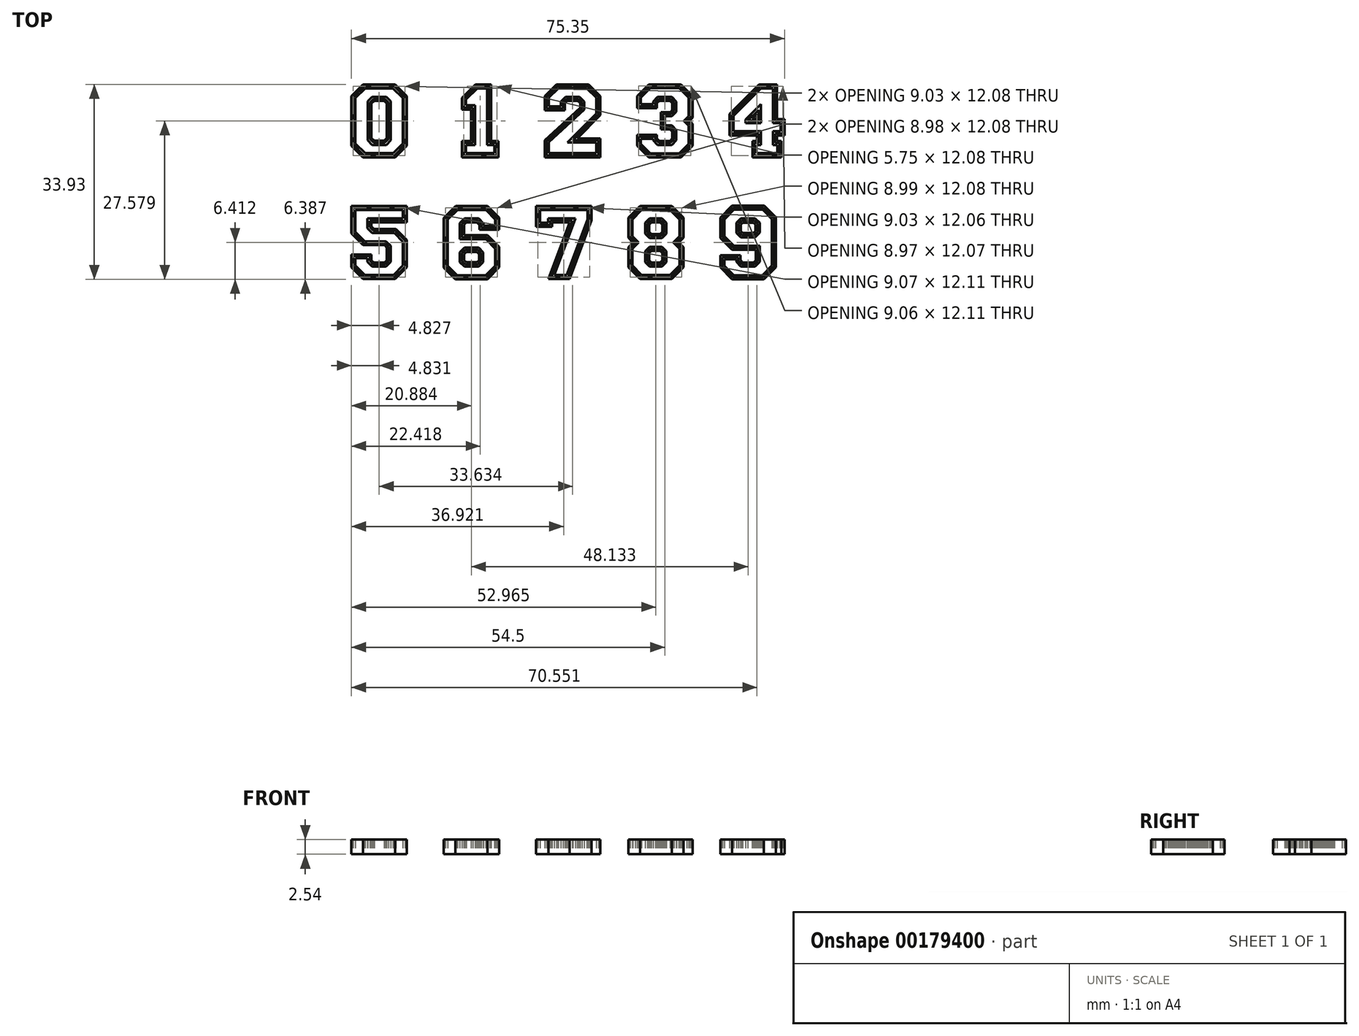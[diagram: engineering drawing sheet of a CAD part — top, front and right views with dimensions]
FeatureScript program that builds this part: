
annotation { "Feature Type Name" : "Feature", "Feature Type Description" : "" }
export const myFeature = defineFeature(function(context is Context, id is Id, definition is map)
    precondition{}
    {
        {
            var Q0;
            Q0=qCreatedBy(makeId("Top.planeOp"),FACE);
            var sketch = newSketch(context, id + "F0", { "sketchPlane" : qUnion([Q0])});
            skLineSegment(sketch, "E0", {"start": v(-43.64, -4.3) * mm, "end": v(-41.6, -2.26) * mm});
            skLineSegment(sketch, "E1", {"start": v(-41.6, -2.26) * mm, "end": v(-36.02, -2.26) * mm});
            skLineSegment(sketch, "E2", {"start": v(-36.02, -2.26) * mm, "end": v(-33.99, -4.3) * mm});
            skLineSegment(sketch, "E3", {"start": v(-33.99, -4.3) * mm, "end": v(-33.99, -12.93) * mm});
            skLineSegment(sketch, "E4", {"start": v(-33.99, -12.93) * mm, "end": v(-36.02, -14.96) * mm});
            skLineSegment(sketch, "E5", {"start": v(-36.02, -14.96) * mm, "end": v(-41.6, -14.96) * mm});
            skLineSegment(sketch, "E6", {"start": v(-41.6, -14.96) * mm, "end": v(-43.64, -12.93) * mm});
            skLineSegment(sketch, "E7", {"start": v(-43.64, -12.93) * mm, "end": v(-43.64, -4.3) * mm});
            skLineSegment(sketch, "E8", {"start": v(-43.33, -4.44) * mm, "end": v(-41.46, -2.57) * mm});
            skLineSegment(sketch, "E9", {"start": v(-41.46, -2.57) * mm, "end": v(-36.17, -2.57) * mm});
            skLineSegment(sketch, "E10", {"start": v(-36.17, -2.57) * mm, "end": v(-34.3, -4.44) * mm});
            skLineSegment(sketch, "E11", {"start": v(-34.3, -4.44) * mm, "end": v(-34.3, -12.78) * mm});
            skLineSegment(sketch, "E12", {"start": v(-34.3, -12.78) * mm, "end": v(-36.17, -14.65) * mm});
            skLineSegment(sketch, "E13", {"start": v(-36.17, -14.65) * mm, "end": v(-41.46, -14.65) * mm});
            skLineSegment(sketch, "E14", {"start": v(-41.46, -14.65) * mm, "end": v(-43.33, -12.78) * mm});
            skLineSegment(sketch, "E15", {"start": v(-43.33, -12.78) * mm, "end": v(-43.33, -4.44) * mm});
            skLineSegment(sketch, "E16", {"start": v(-42.93, -4.64) * mm, "end": v(-41.26, -2.97) * mm});
            skLineSegment(sketch, "E17", {"start": v(-41.26, -2.97) * mm, "end": v(-36.38, -2.97) * mm});
            skLineSegment(sketch, "E18", {"start": v(-36.38, -2.97) * mm, "end": v(-34.68, -4.66) * mm});
            skLineSegment(sketch, "E19", {"start": v(-34.68, -4.66) * mm, "end": v(-34.68, -12.58) * mm});
            skLineSegment(sketch, "E20", {"start": v(-34.68, -12.58) * mm, "end": v(-36.35, -14.25) * mm});
            skLineSegment(sketch, "E21", {"start": v(-36.35, -14.25) * mm, "end": v(-41.26, -14.25) * mm});
            skLineSegment(sketch, "E22", {"start": v(-41.26, -14.25) * mm, "end": v(-42.93, -12.58) * mm});
            skLineSegment(sketch, "E23", {"start": v(-42.93, -12.58) * mm, "end": v(-42.93, -4.64) * mm});
            skLineSegment(sketch, "E24", {"start": v(-40.8, -5.2) * mm, "end": v(-40.06, -4.46) * mm});
            skLineSegment(sketch, "E25", {"start": v(-40.06, -4.46) * mm, "end": v(-37.54, -4.46) * mm});
            skLineSegment(sketch, "E26", {"start": v(-37.54, -4.46) * mm, "end": v(-36.8, -5.2) * mm});
            skLineSegment(sketch, "E27", {"start": v(-36.8, -5.2) * mm, "end": v(-36.8, -12.02) * mm});
            skLineSegment(sketch, "E28", {"start": v(-36.8, -12.02) * mm, "end": v(-37.58, -12.8) * mm});
            skLineSegment(sketch, "E29", {"start": v(-37.58, -12.8) * mm, "end": v(-40.03, -12.8) * mm});
            skLineSegment(sketch, "E30", {"start": v(-40.03, -12.8) * mm, "end": v(-40.8, -12.02) * mm});
            skLineSegment(sketch, "E31", {"start": v(-40.8, -12.02) * mm, "end": v(-40.8, -5.2) * mm});
            skLineSegment(sketch, "E32", {"start": v(-40.45, -5.46) * mm, "end": v(-39.81, -4.82) * mm});
            skLineSegment(sketch, "E33", {"start": v(-39.81, -4.82) * mm, "end": v(-37.82, -4.82) * mm});
            skLineSegment(sketch, "E34", {"start": v(-37.82, -4.82) * mm, "end": v(-37.18, -5.46) * mm});
            skLineSegment(sketch, "E35", {"start": v(-37.18, -5.46) * mm, "end": v(-37.18, -11.77) * mm});
            skLineSegment(sketch, "E36", {"start": v(-37.18, -11.77) * mm, "end": v(-37.82, -12.4) * mm});
            skLineSegment(sketch, "E37", {"start": v(-37.82, -12.4) * mm, "end": v(-39.81, -12.4) * mm});
            skLineSegment(sketch, "E38", {"start": v(-39.81, -12.4) * mm, "end": v(-40.45, -11.77) * mm});
            skLineSegment(sketch, "E39", {"start": v(-40.45, -11.77) * mm, "end": v(-40.45, -5.46) * mm});
            skLineSegment(sketch, "E40", {"start": v(-40.14, -5.58) * mm, "end": v(-39.68, -5.13) * mm});
            skLineSegment(sketch, "E41", {"start": v(-39.68, -5.13) * mm, "end": v(-37.94, -5.13) * mm});
            skLineSegment(sketch, "E42", {"start": v(-37.94, -5.13) * mm, "end": v(-37.49, -5.58) * mm});
            skLineSegment(sketch, "E43", {"start": v(-37.49, -5.58) * mm, "end": v(-37.49, -11.64) * mm});
            skLineSegment(sketch, "E44", {"start": v(-37.49, -11.64) * mm, "end": v(-37.94, -12.1) * mm});
            skLineSegment(sketch, "E45", {"start": v(-37.94, -12.1) * mm, "end": v(-39.68, -12.1) * mm});
            skLineSegment(sketch, "E46", {"start": v(-39.68, -12.1) * mm, "end": v(-40.14, -11.64) * mm});
            skLineSegment(sketch, "E47", {"start": v(-40.14, -11.64) * mm, "end": v(-40.14, -5.58) * mm});
            skLineSegment(sketch, "E48", {"start": v(-19.33, -2.26) * mm, "end": v(-19.33, -12.11) * mm});
            skLineSegment(sketch, "E49", {"start": v(-19.33, -12.11) * mm, "end": v(-18.06, -12.11) * mm});
            skLineSegment(sketch, "E50", {"start": v(-18.06, -12.11) * mm, "end": v(-18.06, -14.96) * mm});
            skLineSegment(sketch, "E51", {"start": v(-18.06, -14.96) * mm, "end": v(-24.4, -14.96) * mm});
            skLineSegment(sketch, "E52", {"start": v(-24.4, -14.96) * mm, "end": v(-24.4, -12.11) * mm});
            skLineSegment(sketch, "E53", {"start": v(-24.4, -12.11) * mm, "end": v(-22.8, -12.11) * mm});
            skLineSegment(sketch, "E54", {"start": v(-22.8, -12.11) * mm, "end": v(-22.8, -6.64) * mm});
            skLineSegment(sketch, "E55", {"start": v(-22.8, -6.64) * mm, "end": v(-24.4, -6.64) * mm});
            skLineSegment(sketch, "E56", {"start": v(-24.4, -6.64) * mm, "end": v(-24.4, -4.62) * mm});
            skLineSegment(sketch, "E57", {"start": v(-24.4, -4.62) * mm, "end": v(-22.05, -2.26) * mm});
            skLineSegment(sketch, "E58", {"start": v(-22.05, -2.26) * mm, "end": v(-19.33, -2.26) * mm});
            skLineSegment(sketch, "E59", {"start": v(-19.62, -2.57) * mm, "end": v(-19.62, -12.42) * mm});
            skLineSegment(sketch, "E60", {"start": v(-19.62, -12.42) * mm, "end": v(-18.35, -12.42) * mm});
            skLineSegment(sketch, "E61", {"start": v(-18.35, -12.42) * mm, "end": v(-18.35, -14.65) * mm});
            skLineSegment(sketch, "E62", {"start": v(-18.35, -14.65) * mm, "end": v(-24.1, -14.65) * mm});
            skLineSegment(sketch, "E63", {"start": v(-24.1, -14.65) * mm, "end": v(-24.1, -12.42) * mm});
            skLineSegment(sketch, "E64", {"start": v(-24.1, -12.42) * mm, "end": v(-22.5, -12.42) * mm});
            skLineSegment(sketch, "E65", {"start": v(-22.5, -12.42) * mm, "end": v(-22.5, -6.33) * mm});
            skLineSegment(sketch, "E66", {"start": v(-22.5, -6.33) * mm, "end": v(-24.1, -6.33) * mm});
            skLineSegment(sketch, "E67", {"start": v(-24.1, -6.33) * mm, "end": v(-24.1, -4.75) * mm});
            skLineSegment(sketch, "E68", {"start": v(-24.1, -4.75) * mm, "end": v(-21.92, -2.57) * mm});
            skLineSegment(sketch, "E69", {"start": v(-21.92, -2.57) * mm, "end": v(-19.62, -2.57) * mm});
            skLineSegment(sketch, "E70", {"start": v(-20.01, -2.97) * mm, "end": v(-20.01, -12.82) * mm});
            skLineSegment(sketch, "E71", {"start": v(-20.01, -12.82) * mm, "end": v(-18.74, -12.82) * mm});
            skLineSegment(sketch, "E72", {"start": v(-18.74, -12.82) * mm, "end": v(-18.74, -14.25) * mm});
            skLineSegment(sketch, "E73", {"start": v(-18.74, -14.25) * mm, "end": v(-23.7, -14.25) * mm});
            skLineSegment(sketch, "E74", {"start": v(-23.7, -14.25) * mm, "end": v(-23.7, -12.82) * mm});
            skLineSegment(sketch, "E75", {"start": v(-23.7, -12.82) * mm, "end": v(-22.1, -12.82) * mm});
            skLineSegment(sketch, "E76", {"start": v(-22.1, -12.82) * mm, "end": v(-22.1, -5.93) * mm});
            skLineSegment(sketch, "E77", {"start": v(-22.1, -5.93) * mm, "end": v(-23.7, -5.93) * mm});
            skLineSegment(sketch, "E78", {"start": v(-23.7, -5.93) * mm, "end": v(-23.7, -4.91) * mm});
            skLineSegment(sketch, "E79", {"start": v(-23.7, -4.91) * mm, "end": v(-21.76, -2.97) * mm});
            skLineSegment(sketch, "E80", {"start": v(-21.76, -2.97) * mm, "end": v(-20.01, -2.97) * mm});
            skLineSegment(sketch, "E81", {"start": v(22.6, -23.39) * mm, "end": v(28.18, -23.39) * mm});
            skLineSegment(sketch, "E82", {"start": v(28.18, -23.39) * mm, "end": v(30.22, -25.43) * mm});
            skLineSegment(sketch, "E83", {"start": v(30.22, -25.43) * mm, "end": v(30.22, -34.07) * mm});
            skLineSegment(sketch, "E84", {"start": v(30.22, -34.07) * mm, "end": v(28.12, -36.17) * mm});
            skLineSegment(sketch, "E85", {"start": v(28.12, -36.17) * mm, "end": v(22.57, -36.17) * mm});
            skLineSegment(sketch, "E86", {"start": v(22.57, -36.17) * mm, "end": v(20.53, -34.1) * mm});
            skLineSegment(sketch, "E87", {"start": v(20.53, -34.1) * mm, "end": v(20.53, -32.02) * mm});
            skLineSegment(sketch, "E88", {"start": v(20.53, -32.02) * mm, "end": v(24.02, -32.02) * mm});
            skLineSegment(sketch, "E89", {"start": v(24.02, -32.02) * mm, "end": v(24.02, -32.85) * mm});
            skLineSegment(sketch, "E90", {"start": v(24.02, -32.85) * mm, "end": v(24.42, -33.27) * mm});
            skLineSegment(sketch, "E91", {"start": v(24.42, -33.27) * mm, "end": v(26.3, -33.27) * mm});
            skLineSegment(sketch, "E92", {"start": v(26.3, -33.27) * mm, "end": v(26.68, -32.88) * mm});
            skLineSegment(sketch, "E93", {"start": v(26.68, -32.88) * mm, "end": v(26.68, -31.05) * mm});
            skLineSegment(sketch, "E94", {"start": v(26.68, -31.05) * mm, "end": v(22.58, -31.05) * mm});
            skLineSegment(sketch, "E95", {"start": v(22.58, -31.05) * mm, "end": v(20.54, -29.01) * mm});
            skLineSegment(sketch, "E96", {"start": v(20.54, -29.01) * mm, "end": v(20.54, -25.46) * mm});
            skLineSegment(sketch, "E97", {"start": v(20.54, -25.46) * mm, "end": v(22.6, -23.39) * mm});
            skLineSegment(sketch, "E98", {"start": v(22.75, -23.74) * mm, "end": v(28.03, -23.74) * mm});
            skLineSegment(sketch, "E99", {"start": v(28.03, -23.74) * mm, "end": v(29.87, -25.58) * mm});
            skLineSegment(sketch, "E100", {"start": v(29.87, -25.58) * mm, "end": v(29.87, -33.92) * mm});
            skLineSegment(sketch, "E101", {"start": v(29.87, -33.92) * mm, "end": v(27.97, -35.82) * mm});
            skLineSegment(sketch, "E102", {"start": v(27.97, -35.82) * mm, "end": v(22.72, -35.82) * mm});
            skLineSegment(sketch, "E103", {"start": v(22.72, -35.82) * mm, "end": v(20.89, -33.96) * mm});
            skLineSegment(sketch, "E104", {"start": v(20.89, -33.96) * mm, "end": v(20.89, -32.37) * mm});
            skLineSegment(sketch, "E105", {"start": v(20.89, -32.37) * mm, "end": v(23.67, -32.37) * mm});
            skLineSegment(sketch, "E106", {"start": v(23.67, -32.37) * mm, "end": v(23.67, -33) * mm});
            skLineSegment(sketch, "E107", {"start": v(23.67, -33) * mm, "end": v(24.27, -33.62) * mm});
            skLineSegment(sketch, "E108", {"start": v(24.27, -33.62) * mm, "end": v(26.46, -33.62) * mm});
            skLineSegment(sketch, "E109", {"start": v(26.46, -33.62) * mm, "end": v(27.04, -33.03) * mm});
            skLineSegment(sketch, "E110", {"start": v(27.04, -33.03) * mm, "end": v(27.04, -30.7) * mm});
            skLineSegment(sketch, "E111", {"start": v(27.04, -30.7) * mm, "end": v(22.72, -30.7) * mm});
            skLineSegment(sketch, "E112", {"start": v(22.72, -30.7) * mm, "end": v(20.9, -28.87) * mm});
            skLineSegment(sketch, "E113", {"start": v(20.9, -28.87) * mm, "end": v(20.9, -25.6) * mm});
            skLineSegment(sketch, "E114", {"start": v(20.9, -25.6) * mm, "end": v(22.75, -23.74) * mm});
            skLineSegment(sketch, "E115", {"start": v(22.9, -24.1) * mm, "end": v(27.89, -24.1) * mm});
            skLineSegment(sketch, "E116", {"start": v(27.89, -24.1) * mm, "end": v(29.51, -25.72) * mm});
            skLineSegment(sketch, "E117", {"start": v(29.51, -25.72) * mm, "end": v(29.51, -33.78) * mm});
            skLineSegment(sketch, "E118", {"start": v(29.51, -33.78) * mm, "end": v(27.82, -35.47) * mm});
            skLineSegment(sketch, "E119", {"start": v(27.82, -35.47) * mm, "end": v(22.87, -35.47) * mm});
            skLineSegment(sketch, "E120", {"start": v(22.87, -35.47) * mm, "end": v(21.24, -33.81) * mm});
            skLineSegment(sketch, "E121", {"start": v(21.24, -33.81) * mm, "end": v(21.24, -32.73) * mm});
            skLineSegment(sketch, "E122", {"start": v(21.24, -32.73) * mm, "end": v(23.31, -32.73) * mm});
            skLineSegment(sketch, "E123", {"start": v(23.31, -32.73) * mm, "end": v(23.31, -33.13) * mm});
            skLineSegment(sketch, "E124", {"start": v(23.31, -33.13) * mm, "end": v(24.12, -33.97) * mm});
            skLineSegment(sketch, "E125", {"start": v(24.12, -33.97) * mm, "end": v(26.6, -33.97) * mm});
            skLineSegment(sketch, "E126", {"start": v(26.6, -33.97) * mm, "end": v(27.39, -33.17) * mm});
            skLineSegment(sketch, "E127", {"start": v(27.39, -33.17) * mm, "end": v(27.39, -30.35) * mm});
            skLineSegment(sketch, "E128", {"start": v(27.39, -30.35) * mm, "end": v(22.87, -30.35) * mm});
            skLineSegment(sketch, "E129", {"start": v(22.87, -30.35) * mm, "end": v(21.25, -28.72) * mm});
            skLineSegment(sketch, "E130", {"start": v(21.25, -28.72) * mm, "end": v(21.25, -25.75) * mm});
            skLineSegment(sketch, "E131", {"start": v(21.25, -25.75) * mm, "end": v(22.9, -24.1) * mm});
            skLineSegment(sketch, "E132", {"start": v(24.12, -25.6) * mm, "end": v(26.6, -25.6) * mm});
            skLineSegment(sketch, "E133", {"start": v(26.6, -25.6) * mm, "end": v(27.4, -26.37) * mm});
            skLineSegment(sketch, "E134", {"start": v(27.4, -26.37) * mm, "end": v(27.4, -28.1) * mm});
            skLineSegment(sketch, "E135", {"start": v(27.4, -28.1) * mm, "end": v(26.6, -28.89) * mm});
            skLineSegment(sketch, "E136", {"start": v(26.6, -28.89) * mm, "end": v(24.11, -28.89) * mm});
            skLineSegment(sketch, "E137", {"start": v(24.11, -28.89) * mm, "end": v(23.33, -28.1) * mm});
            skLineSegment(sketch, "E138", {"start": v(23.33, -28.1) * mm, "end": v(23.33, -26.37) * mm});
            skLineSegment(sketch, "E139", {"start": v(23.33, -26.37) * mm, "end": v(24.12, -25.6) * mm});
            skLineSegment(sketch, "E140", {"start": v(24.27, -25.98) * mm, "end": v(26.45, -25.98) * mm});
            skLineSegment(sketch, "E141", {"start": v(26.45, -25.98) * mm, "end": v(27.02, -26.53) * mm});
            skLineSegment(sketch, "E142", {"start": v(27.02, -26.53) * mm, "end": v(27.02, -27.94) * mm});
            skLineSegment(sketch, "E143", {"start": v(27.02, -27.94) * mm, "end": v(26.44, -28.52) * mm});
            skLineSegment(sketch, "E144", {"start": v(26.44, -28.52) * mm, "end": v(24.27, -28.52) * mm});
            skLineSegment(sketch, "E145", {"start": v(24.27, -28.52) * mm, "end": v(23.7, -27.95) * mm});
            skLineSegment(sketch, "E146", {"start": v(23.7, -27.95) * mm, "end": v(23.7, -26.53) * mm});
            skLineSegment(sketch, "E147", {"start": v(23.7, -26.53) * mm, "end": v(24.27, -25.98) * mm});
            skLineSegment(sketch, "E148", {"start": v(24.42, -26.36) * mm, "end": v(26.3, -26.36) * mm});
            skLineSegment(sketch, "E149", {"start": v(26.3, -26.36) * mm, "end": v(26.65, -26.69) * mm});
            skLineSegment(sketch, "E150", {"start": v(26.65, -26.69) * mm, "end": v(26.65, -27.78) * mm});
            skLineSegment(sketch, "E151", {"start": v(26.65, -27.78) * mm, "end": v(26.29, -28.14) * mm});
            skLineSegment(sketch, "E152", {"start": v(26.29, -28.14) * mm, "end": v(24.42, -28.14) * mm});
            skLineSegment(sketch, "E153", {"start": v(24.42, -28.14) * mm, "end": v(24.08, -27.8) * mm});
            skLineSegment(sketch, "E154", {"start": v(24.08, -27.8) * mm, "end": v(24.08, -26.68) * mm});
            skLineSegment(sketch, "E155", {"start": v(24.08, -26.68) * mm, "end": v(24.42, -26.36) * mm});
            skLineSegment(sketch, "E156", {"start": v(-19.98, -36.2) * mm, "end": v(-25.56, -36.2) * mm});
            skLineSegment(sketch, "E157", {"start": v(-25.56, -36.2) * mm, "end": v(-27.6, -34.15) * mm});
            skLineSegment(sketch, "E158", {"start": v(-27.6, -34.15) * mm, "end": v(-27.6, -25.52) * mm});
            skLineSegment(sketch, "E159", {"start": v(-27.6, -25.52) * mm, "end": v(-25.5, -23.41) * mm});
            skLineSegment(sketch, "E160", {"start": v(-25.5, -23.41) * mm, "end": v(-19.95, -23.41) * mm});
            skLineSegment(sketch, "E161", {"start": v(-19.95, -23.41) * mm, "end": v(-17.91, -25.48) * mm});
            skLineSegment(sketch, "E162", {"start": v(-17.91, -25.48) * mm, "end": v(-17.91, -27.56) * mm});
            skLineSegment(sketch, "E163", {"start": v(-17.91, -27.56) * mm, "end": v(-21.4, -27.56) * mm});
            skLineSegment(sketch, "E164", {"start": v(-21.4, -27.56) * mm, "end": v(-21.4, -26.73) * mm});
            skLineSegment(sketch, "E165", {"start": v(-21.4, -26.73) * mm, "end": v(-21.8, -26.32) * mm});
            skLineSegment(sketch, "E166", {"start": v(-21.8, -26.32) * mm, "end": v(-23.69, -26.32) * mm});
            skLineSegment(sketch, "E167", {"start": v(-23.69, -26.32) * mm, "end": v(-24.06, -26.7) * mm});
            skLineSegment(sketch, "E168", {"start": v(-24.06, -26.7) * mm, "end": v(-24.06, -28.53) * mm});
            skLineSegment(sketch, "E169", {"start": v(-24.06, -28.53) * mm, "end": v(-19.96, -28.53) * mm});
            skLineSegment(sketch, "E170", {"start": v(-19.96, -28.53) * mm, "end": v(-17.92, -30.57) * mm});
            skLineSegment(sketch, "E171", {"start": v(-17.92, -30.57) * mm, "end": v(-17.92, -34.12) * mm});
            skLineSegment(sketch, "E172", {"start": v(-17.92, -34.12) * mm, "end": v(-19.98, -36.2) * mm});
            skLineSegment(sketch, "E173", {"start": v(-20.13, -35.84) * mm, "end": v(-25.41, -35.84) * mm});
            skLineSegment(sketch, "E174", {"start": v(-25.41, -35.84) * mm, "end": v(-27.25, -34) * mm});
            skLineSegment(sketch, "E175", {"start": v(-27.25, -34) * mm, "end": v(-27.25, -25.66) * mm});
            skLineSegment(sketch, "E176", {"start": v(-27.25, -25.66) * mm, "end": v(-25.35, -23.77) * mm});
            skLineSegment(sketch, "E177", {"start": v(-25.35, -23.77) * mm, "end": v(-20.1, -23.77) * mm});
            skLineSegment(sketch, "E178", {"start": v(-20.1, -23.77) * mm, "end": v(-18.27, -25.63) * mm});
            skLineSegment(sketch, "E179", {"start": v(-18.27, -25.63) * mm, "end": v(-18.27, -27.2) * mm});
            skLineSegment(sketch, "E180", {"start": v(-18.27, -27.2) * mm, "end": v(-21.05, -27.2) * mm});
            skLineSegment(sketch, "E181", {"start": v(-21.05, -27.2) * mm, "end": v(-21.05, -26.6) * mm});
            skLineSegment(sketch, "E182", {"start": v(-21.05, -26.6) * mm, "end": v(-21.65, -25.96) * mm});
            skLineSegment(sketch, "E183", {"start": v(-21.65, -25.96) * mm, "end": v(-23.84, -25.96) * mm});
            skLineSegment(sketch, "E184", {"start": v(-23.84, -25.96) * mm, "end": v(-24.42, -26.56) * mm});
            skLineSegment(sketch, "E185", {"start": v(-24.42, -26.56) * mm, "end": v(-24.42, -28.88) * mm});
            skLineSegment(sketch, "E186", {"start": v(-24.42, -28.88) * mm, "end": v(-20.1, -28.88) * mm});
            skLineSegment(sketch, "E187", {"start": v(-20.1, -28.88) * mm, "end": v(-18.27, -30.71) * mm});
            skLineSegment(sketch, "E188", {"start": v(-18.27, -30.71) * mm, "end": v(-18.27, -33.98) * mm});
            skLineSegment(sketch, "E189", {"start": v(-18.27, -33.98) * mm, "end": v(-20.13, -35.84) * mm});
            skLineSegment(sketch, "E190", {"start": v(-20.27, -35.49) * mm, "end": v(-25.27, -35.49) * mm});
            skLineSegment(sketch, "E191", {"start": v(-25.27, -35.49) * mm, "end": v(-26.9, -33.86) * mm});
            skLineSegment(sketch, "E192", {"start": v(-26.9, -33.86) * mm, "end": v(-26.9, -25.8) * mm});
            skLineSegment(sketch, "E193", {"start": v(-26.9, -25.8) * mm, "end": v(-25.2, -24.12) * mm});
            skLineSegment(sketch, "E194", {"start": v(-25.2, -24.12) * mm, "end": v(-20.25, -24.12) * mm});
            skLineSegment(sketch, "E195", {"start": v(-20.25, -24.12) * mm, "end": v(-18.62, -25.77) * mm});
            skLineSegment(sketch, "E196", {"start": v(-18.62, -25.77) * mm, "end": v(-18.62, -26.86) * mm});
            skLineSegment(sketch, "E197", {"start": v(-18.62, -26.86) * mm, "end": v(-20.7, -26.86) * mm});
            skLineSegment(sketch, "E198", {"start": v(-20.7, -26.86) * mm, "end": v(-20.7, -26.45) * mm});
            skLineSegment(sketch, "E199", {"start": v(-20.7, -26.45) * mm, "end": v(-21.5, -25.61) * mm});
            skLineSegment(sketch, "E200", {"start": v(-21.5, -25.61) * mm, "end": v(-23.98, -25.61) * mm});
            skLineSegment(sketch, "E201", {"start": v(-23.98, -25.61) * mm, "end": v(-24.77, -26.41) * mm});
            skLineSegment(sketch, "E202", {"start": v(-24.77, -26.41) * mm, "end": v(-24.77, -29.24) * mm});
            skLineSegment(sketch, "E203", {"start": v(-24.77, -29.24) * mm, "end": v(-20.25, -29.24) * mm});
            skLineSegment(sketch, "E204", {"start": v(-20.25, -29.24) * mm, "end": v(-18.62, -30.86) * mm});
            skLineSegment(sketch, "E205", {"start": v(-18.62, -30.86) * mm, "end": v(-18.62, -33.83) * mm});
            skLineSegment(sketch, "E206", {"start": v(-18.62, -33.83) * mm, "end": v(-20.27, -35.49) * mm});
            skLineSegment(sketch, "E207", {"start": v(-21.5, -33.98) * mm, "end": v(-23.98, -33.98) * mm});
            skLineSegment(sketch, "E208", {"start": v(-23.98, -33.98) * mm, "end": v(-24.78, -33.22) * mm});
            skLineSegment(sketch, "E209", {"start": v(-24.78, -33.22) * mm, "end": v(-24.78, -31.5) * mm});
            skLineSegment(sketch, "E210", {"start": v(-24.78, -31.5) * mm, "end": v(-23.98, -30.7) * mm});
            skLineSegment(sketch, "E211", {"start": v(-23.98, -30.7) * mm, "end": v(-21.5, -30.7) * mm});
            skLineSegment(sketch, "E212", {"start": v(-21.5, -30.7) * mm, "end": v(-20.71, -31.47) * mm});
            skLineSegment(sketch, "E213", {"start": v(-20.71, -31.47) * mm, "end": v(-20.71, -33.22) * mm});
            skLineSegment(sketch, "E214", {"start": v(-20.71, -33.22) * mm, "end": v(-21.5, -33.98) * mm});
            skLineSegment(sketch, "E215", {"start": v(-21.65, -33.6) * mm, "end": v(-23.83, -33.6) * mm});
            skLineSegment(sketch, "E216", {"start": v(-23.83, -33.6) * mm, "end": v(-24.4, -33.05) * mm});
            skLineSegment(sketch, "E217", {"start": v(-24.4, -33.05) * mm, "end": v(-24.4, -31.65) * mm});
            skLineSegment(sketch, "E218", {"start": v(-24.4, -31.65) * mm, "end": v(-23.82, -31.07) * mm});
            skLineSegment(sketch, "E219", {"start": v(-23.82, -31.07) * mm, "end": v(-21.65, -31.07) * mm});
            skLineSegment(sketch, "E220", {"start": v(-21.65, -31.07) * mm, "end": v(-21.09, -31.63) * mm});
            skLineSegment(sketch, "E221", {"start": v(-21.09, -31.63) * mm, "end": v(-21.09, -33.06) * mm});
            skLineSegment(sketch, "E222", {"start": v(-21.09, -33.06) * mm, "end": v(-21.65, -33.6) * mm});
            skLineSegment(sketch, "E223", {"start": v(-21.8, -33.23) * mm, "end": v(-23.68, -33.23) * mm});
            skLineSegment(sketch, "E224", {"start": v(-23.68, -33.23) * mm, "end": v(-24.03, -32.9) * mm});
            skLineSegment(sketch, "E225", {"start": v(-24.03, -32.9) * mm, "end": v(-24.03, -31.8) * mm});
            skLineSegment(sketch, "E226", {"start": v(-24.03, -31.8) * mm, "end": v(-23.67, -31.44) * mm});
            skLineSegment(sketch, "E227", {"start": v(-23.67, -31.44) * mm, "end": v(-21.8, -31.44) * mm});
            skLineSegment(sketch, "E228", {"start": v(-21.8, -31.44) * mm, "end": v(-21.46, -31.78) * mm});
            skLineSegment(sketch, "E229", {"start": v(-21.46, -31.78) * mm, "end": v(-21.46, -32.9) * mm});
            skLineSegment(sketch, "E230", {"start": v(-21.46, -32.9) * mm, "end": v(-21.8, -33.23) * mm});
            skLineSegment(sketch, "E231", {"start": v(-10, -6.82) * mm, "end": v(-10, -4.3) * mm});
            skLineSegment(sketch, "E232", {"start": v(-10, -4.3) * mm, "end": v(-7.97, -2.26) * mm});
            skLineSegment(sketch, "E233", {"start": v(-7.97, -2.26) * mm, "end": v(-2.39, -2.26) * mm});
            skLineSegment(sketch, "E234", {"start": v(-2.39, -2.26) * mm, "end": v(-0.35, -4.3) * mm});
            skLineSegment(sketch, "E235", {"start": v(-0.35, -4.3) * mm, "end": v(-0.35, -7.65) * mm});
            skLineSegment(sketch, "E236", {"start": v(-0.35, -7.65) * mm, "end": v(-4.38, -11.68) * mm});
            skLineSegment(sketch, "E237", {"start": v(-4.38, -11.68) * mm, "end": v(-0.35, -11.68) * mm});
            skLineSegment(sketch, "E238", {"start": v(-0.35, -11.68) * mm, "end": v(-0.35, -14.96) * mm});
            skLineSegment(sketch, "E239", {"start": v(-0.35, -14.96) * mm, "end": v(-10, -14.96) * mm});
            skLineSegment(sketch, "E240", {"start": v(-10, -14.96) * mm, "end": v(-10, -12) * mm});
            skLineSegment(sketch, "E241", {"start": v(-10, -12) * mm, "end": v(-3.85, -6.36) * mm});
            skLineSegment(sketch, "E242", {"start": v(-3.85, -6.36) * mm, "end": v(-3.85, -5.55) * mm});
            skLineSegment(sketch, "E243", {"start": v(-3.85, -5.55) * mm, "end": v(-4.27, -5.13) * mm});
            skLineSegment(sketch, "E244", {"start": v(-4.27, -5.13) * mm, "end": v(-6.1, -5.13) * mm});
            skLineSegment(sketch, "E245", {"start": v(-6.1, -5.13) * mm, "end": v(-6.52, -5.55) * mm});
            skLineSegment(sketch, "E246", {"start": v(-6.52, -5.55) * mm, "end": v(-6.52, -6.82) * mm});
            skLineSegment(sketch, "E247", {"start": v(-6.52, -6.82) * mm, "end": v(-10, -6.82) * mm});
            skLineSegment(sketch, "E248", {"start": v(-9.7, -6.5) * mm, "end": v(-9.7, -4.42) * mm});
            skLineSegment(sketch, "E249", {"start": v(-9.7, -4.42) * mm, "end": v(-7.84, -2.57) * mm});
            skLineSegment(sketch, "E250", {"start": v(-7.84, -2.57) * mm, "end": v(-2.51, -2.57) * mm});
            skLineSegment(sketch, "E251", {"start": v(-2.51, -2.57) * mm, "end": v(-0.66, -4.42) * mm});
            skLineSegment(sketch, "E252", {"start": v(-0.66, -4.42) * mm, "end": v(-0.66, -7.52) * mm});
            skLineSegment(sketch, "E253", {"start": v(-0.66, -7.52) * mm, "end": v(-5.12, -11.98) * mm});
            skLineSegment(sketch, "E254", {"start": v(-5.12, -11.98) * mm, "end": v(-0.66, -11.98) * mm});
            skLineSegment(sketch, "E255", {"start": v(-0.66, -11.98) * mm, "end": v(-0.66, -14.65) * mm});
            skLineSegment(sketch, "E256", {"start": v(-0.66, -14.65) * mm, "end": v(-9.7, -14.65) * mm});
            skLineSegment(sketch, "E257", {"start": v(-9.7, -14.65) * mm, "end": v(-9.7, -12.14) * mm});
            skLineSegment(sketch, "E258", {"start": v(-9.7, -12.14) * mm, "end": v(-3.55, -6.5) * mm});
            skLineSegment(sketch, "E259", {"start": v(-3.55, -6.5) * mm, "end": v(-3.55, -5.42) * mm});
            skLineSegment(sketch, "E260", {"start": v(-3.55, -5.42) * mm, "end": v(-4.14, -4.82) * mm});
            skLineSegment(sketch, "E261", {"start": v(-4.14, -4.82) * mm, "end": v(-6.23, -4.82) * mm});
            skLineSegment(sketch, "E262", {"start": v(-6.23, -4.82) * mm, "end": v(-6.83, -5.42) * mm});
            skLineSegment(sketch, "E263", {"start": v(-6.83, -5.42) * mm, "end": v(-6.83, -6.5) * mm});
            skLineSegment(sketch, "E264", {"start": v(-6.83, -6.5) * mm, "end": v(-9.7, -6.5) * mm});
            skLineSegment(sketch, "E265", {"start": v(-9.3, -6.1) * mm, "end": v(-9.3, -4.59) * mm});
            skLineSegment(sketch, "E266", {"start": v(-9.3, -4.59) * mm, "end": v(-7.68, -2.97) * mm});
            skLineSegment(sketch, "E267", {"start": v(-7.68, -2.97) * mm, "end": v(-2.68, -2.97) * mm});
            skLineSegment(sketch, "E268", {"start": v(-2.68, -2.97) * mm, "end": v(-1.06, -4.59) * mm});
            skLineSegment(sketch, "E269", {"start": v(-1.06, -4.59) * mm, "end": v(-1.06, -7.36) * mm});
            skLineSegment(sketch, "E270", {"start": v(-1.06, -7.36) * mm, "end": v(-6.08, -12.38) * mm});
            skLineSegment(sketch, "E271", {"start": v(-6.08, -12.38) * mm, "end": v(-1.06, -12.38) * mm});
            skLineSegment(sketch, "E272", {"start": v(-1.06, -12.38) * mm, "end": v(-1.06, -14.25) * mm});
            skLineSegment(sketch, "E273", {"start": v(-1.06, -14.25) * mm, "end": v(-9.3, -14.25) * mm});
            skLineSegment(sketch, "E274", {"start": v(-9.3, -14.25) * mm, "end": v(-9.3, -12.31) * mm});
            skLineSegment(sketch, "E275", {"start": v(-9.3, -12.31) * mm, "end": v(-3.15, -6.67) * mm});
            skLineSegment(sketch, "E276", {"start": v(-3.15, -6.67) * mm, "end": v(-3.15, -5.25) * mm});
            skLineSegment(sketch, "E277", {"start": v(-3.15, -5.25) * mm, "end": v(-3.98, -4.42) * mm});
            skLineSegment(sketch, "E278", {"start": v(-3.98, -4.42) * mm, "end": v(-6.4, -4.42) * mm});
            skLineSegment(sketch, "E279", {"start": v(-6.4, -4.42) * mm, "end": v(-7.23, -5.25) * mm});
            skLineSegment(sketch, "E280", {"start": v(-7.23, -5.25) * mm, "end": v(-7.23, -6.1) * mm});
            skLineSegment(sketch, "E281", {"start": v(-7.23, -6.1) * mm, "end": v(-9.3, -6.1) * mm});
            skLineSegment(sketch, "E282", {"start": v(6.03, -6.4) * mm, "end": v(6.03, -4.3) * mm});
            skLineSegment(sketch, "E283", {"start": v(6.03, -4.3) * mm, "end": v(8.07, -2.26) * mm});
            skLineSegment(sketch, "E284", {"start": v(8.07, -2.26) * mm, "end": v(13.65, -2.26) * mm});
            skLineSegment(sketch, "E285", {"start": v(13.65, -2.26) * mm, "end": v(15.69, -4.3) * mm});
            skLineSegment(sketch, "E286", {"start": v(15.69, -4.3) * mm, "end": v(15.69, -8.07) * mm});
            skLineSegment(sketch, "E287", {"start": v(15.69, -8.07) * mm, "end": v(15.14, -8.61) * mm});
            skLineSegment(sketch, "E288", {"start": v(15.14, -8.61) * mm, "end": v(15.69, -9.16) * mm});
            skLineSegment(sketch, "E289", {"start": v(15.69, -9.16) * mm, "end": v(15.69, -12.93) * mm});
            skLineSegment(sketch, "E290", {"start": v(15.69, -12.93) * mm, "end": v(13.65, -14.96) * mm});
            skLineSegment(sketch, "E291", {"start": v(13.65, -14.96) * mm, "end": v(8.07, -14.96) * mm});
            skLineSegment(sketch, "E292", {"start": v(8.07, -14.96) * mm, "end": v(6.04, -12.93) * mm});
            skLineSegment(sketch, "E293", {"start": v(6.04, -12.93) * mm, "end": v(6.04, -11.08) * mm});
            skLineSegment(sketch, "E294", {"start": v(6.04, -11.08) * mm, "end": v(9.52, -11.08) * mm});
            skLineSegment(sketch, "E295", {"start": v(9.52, -11.08) * mm, "end": v(9.52, -11.7) * mm});
            skLineSegment(sketch, "E296", {"start": v(9.52, -11.7) * mm, "end": v(9.94, -12.11) * mm});
            skLineSegment(sketch, "E297", {"start": v(9.94, -12.11) * mm, "end": v(11.79, -12.11) * mm});
            skLineSegment(sketch, "E298", {"start": v(11.79, -12.11) * mm, "end": v(12.19, -11.71) * mm});
            skLineSegment(sketch, "E299", {"start": v(12.19, -11.71) * mm, "end": v(12.19, -10.48) * mm});
            skLineSegment(sketch, "E300", {"start": v(12.19, -10.48) * mm, "end": v(11.79, -10.08) * mm});
            skLineSegment(sketch, "E301", {"start": v(11.79, -10.08) * mm, "end": v(10.2, -10.08) * mm});
            skLineSegment(sketch, "E302", {"start": v(10.2, -10.08) * mm, "end": v(10.2, -7.14) * mm});
            skLineSegment(sketch, "E303", {"start": v(10.2, -7.14) * mm, "end": v(11.82, -7.14) * mm});
            skLineSegment(sketch, "E304", {"start": v(11.82, -7.14) * mm, "end": v(12.19, -6.76) * mm});
            skLineSegment(sketch, "E305", {"start": v(12.19, -6.76) * mm, "end": v(12.19, -5.53) * mm});
            skLineSegment(sketch, "E306", {"start": v(12.19, -5.53) * mm, "end": v(11.79, -5.13) * mm});
            skLineSegment(sketch, "E307", {"start": v(11.79, -5.13) * mm, "end": v(9.92, -5.13) * mm});
            skLineSegment(sketch, "E308", {"start": v(9.92, -5.13) * mm, "end": v(9.52, -5.53) * mm});
            skLineSegment(sketch, "E309", {"start": v(9.52, -5.53) * mm, "end": v(9.52, -6.4) * mm});
            skLineSegment(sketch, "E310", {"start": v(9.52, -6.4) * mm, "end": v(6.03, -6.4) * mm});
            skLineSegment(sketch, "E311", {"start": v(6.33, -6.1) * mm, "end": v(6.33, -4.42) * mm});
            skLineSegment(sketch, "E312", {"start": v(6.33, -4.42) * mm, "end": v(8.2, -2.56) * mm});
            skLineSegment(sketch, "E313", {"start": v(8.2, -2.56) * mm, "end": v(13.53, -2.56) * mm});
            skLineSegment(sketch, "E314", {"start": v(13.53, -2.56) * mm, "end": v(15.4, -4.42) * mm});
            skLineSegment(sketch, "E315", {"start": v(15.4, -4.42) * mm, "end": v(15.4, -7.95) * mm});
            skLineSegment(sketch, "E316", {"start": v(15.4, -7.95) * mm, "end": v(14.73, -8.61) * mm});
            skLineSegment(sketch, "E317", {"start": v(14.73, -8.61) * mm, "end": v(15.4, -9.28) * mm});
            skLineSegment(sketch, "E318", {"start": v(15.4, -9.28) * mm, "end": v(15.4, -12.8) * mm});
            skLineSegment(sketch, "E319", {"start": v(15.4, -12.8) * mm, "end": v(13.53, -14.66) * mm});
            skLineSegment(sketch, "E320", {"start": v(13.53, -14.66) * mm, "end": v(8.2, -14.66) * mm});
            skLineSegment(sketch, "E321", {"start": v(8.2, -14.66) * mm, "end": v(6.33, -12.8) * mm});
            skLineSegment(sketch, "E322", {"start": v(6.33, -12.8) * mm, "end": v(6.33, -11.37) * mm});
            skLineSegment(sketch, "E323", {"start": v(6.33, -11.37) * mm, "end": v(9.23, -11.37) * mm});
            skLineSegment(sketch, "E324", {"start": v(9.23, -11.37) * mm, "end": v(9.23, -11.82) * mm});
            skLineSegment(sketch, "E325", {"start": v(9.23, -11.82) * mm, "end": v(9.81, -12.4) * mm});
            skLineSegment(sketch, "E326", {"start": v(9.81, -12.4) * mm, "end": v(11.9, -12.4) * mm});
            skLineSegment(sketch, "E327", {"start": v(11.9, -12.4) * mm, "end": v(12.48, -11.83) * mm});
            skLineSegment(sketch, "E328", {"start": v(12.48, -11.83) * mm, "end": v(12.48, -10.36) * mm});
            skLineSegment(sketch, "E329", {"start": v(12.48, -10.36) * mm, "end": v(11.9, -9.79) * mm});
            skLineSegment(sketch, "E330", {"start": v(11.9, -9.79) * mm, "end": v(10.5, -9.79) * mm});
            skLineSegment(sketch, "E331", {"start": v(10.5, -9.79) * mm, "end": v(10.5, -7.44) * mm});
            skLineSegment(sketch, "E332", {"start": v(10.5, -7.44) * mm, "end": v(11.95, -7.44) * mm});
            skLineSegment(sketch, "E333", {"start": v(11.95, -7.44) * mm, "end": v(12.48, -6.88) * mm});
            skLineSegment(sketch, "E334", {"start": v(12.48, -6.88) * mm, "end": v(12.48, -5.4) * mm});
            skLineSegment(sketch, "E335", {"start": v(12.48, -5.4) * mm, "end": v(11.9, -4.84) * mm});
            skLineSegment(sketch, "E336", {"start": v(11.9, -4.84) * mm, "end": v(9.8, -4.84) * mm});
            skLineSegment(sketch, "E337", {"start": v(9.8, -4.84) * mm, "end": v(9.23, -5.4) * mm});
            skLineSegment(sketch, "E338", {"start": v(9.23, -5.4) * mm, "end": v(9.23, -6.1) * mm});
            skLineSegment(sketch, "E339", {"start": v(9.23, -6.1) * mm, "end": v(6.33, -6.1) * mm});
            skLineSegment(sketch, "E340", {"start": v(6.72, -5.71) * mm, "end": v(6.72, -4.58) * mm});
            skLineSegment(sketch, "E341", {"start": v(6.72, -4.58) * mm, "end": v(8.35, -2.95) * mm});
            skLineSegment(sketch, "E342", {"start": v(8.35, -2.95) * mm, "end": v(13.37, -2.95) * mm});
            skLineSegment(sketch, "E343", {"start": v(13.37, -2.95) * mm, "end": v(15, -4.58) * mm});
            skLineSegment(sketch, "E344", {"start": v(15, -4.58) * mm, "end": v(15, -7.78) * mm});
            skLineSegment(sketch, "E345", {"start": v(15, -7.78) * mm, "end": v(14.17, -8.61) * mm});
            skLineSegment(sketch, "E346", {"start": v(14.17, -8.61) * mm, "end": v(15, -9.44) * mm});
            skLineSegment(sketch, "E347", {"start": v(15, -9.44) * mm, "end": v(15, -12.64) * mm});
            skLineSegment(sketch, "E348", {"start": v(15, -12.64) * mm, "end": v(13.37, -14.27) * mm});
            skLineSegment(sketch, "E349", {"start": v(13.37, -14.27) * mm, "end": v(8.35, -14.27) * mm});
            skLineSegment(sketch, "E350", {"start": v(8.35, -14.27) * mm, "end": v(6.73, -12.64) * mm});
            skLineSegment(sketch, "E351", {"start": v(6.73, -12.64) * mm, "end": v(6.73, -11.77) * mm});
            skLineSegment(sketch, "E352", {"start": v(6.73, -11.77) * mm, "end": v(8.83, -11.77) * mm});
            skLineSegment(sketch, "E353", {"start": v(8.83, -11.77) * mm, "end": v(8.83, -11.98) * mm});
            skLineSegment(sketch, "E354", {"start": v(8.83, -11.98) * mm, "end": v(9.65, -12.8) * mm});
            skLineSegment(sketch, "E355", {"start": v(9.65, -12.8) * mm, "end": v(12.07, -12.8) * mm});
            skLineSegment(sketch, "E356", {"start": v(12.07, -12.8) * mm, "end": v(12.87, -12) * mm});
            skLineSegment(sketch, "E357", {"start": v(12.87, -12) * mm, "end": v(12.87, -10.2) * mm});
            skLineSegment(sketch, "E358", {"start": v(12.87, -10.2) * mm, "end": v(12.07, -9.4) * mm});
            skLineSegment(sketch, "E359", {"start": v(12.07, -9.4) * mm, "end": v(10.9, -9.4) * mm});
            skLineSegment(sketch, "E360", {"start": v(10.9, -9.4) * mm, "end": v(10.9, -7.83) * mm});
            skLineSegment(sketch, "E361", {"start": v(10.9, -7.83) * mm, "end": v(12.12, -7.83) * mm});
            skLineSegment(sketch, "E362", {"start": v(12.12, -7.83) * mm, "end": v(12.87, -7.04) * mm});
            skLineSegment(sketch, "E363", {"start": v(12.87, -7.04) * mm, "end": v(12.87, -5.24) * mm});
            skLineSegment(sketch, "E364", {"start": v(12.87, -5.24) * mm, "end": v(12.07, -4.44) * mm});
            skLineSegment(sketch, "E365", {"start": v(12.07, -4.44) * mm, "end": v(9.63, -4.44) * mm});
            skLineSegment(sketch, "E366", {"start": v(9.63, -4.44) * mm, "end": v(8.83, -5.24) * mm});
            skLineSegment(sketch, "E367", {"start": v(8.83, -5.24) * mm, "end": v(8.83, -5.71) * mm});
            skLineSegment(sketch, "E368", {"start": v(8.83, -5.71) * mm, "end": v(6.72, -5.71) * mm});
            skLineSegment(sketch, "E369", {"start": v(22.11, -11.15) * mm, "end": v(22.11, -7.43) * mm});
            skLineSegment(sketch, "E370", {"start": v(22.11, -7.43) * mm, "end": v(27.28, -2.26) * mm});
            skLineSegment(sketch, "E371", {"start": v(27.28, -2.26) * mm, "end": v(30.38, -2.26) * mm});
            skLineSegment(sketch, "E372", {"start": v(30.38, -2.26) * mm, "end": v(30.38, -8.3) * mm});
            skLineSegment(sketch, "E373", {"start": v(30.38, -8.3) * mm, "end": v(31.7, -8.3) * mm});
            skLineSegment(sketch, "E374", {"start": v(31.7, -8.3) * mm, "end": v(31.7, -11.15) * mm});
            skLineSegment(sketch, "E375", {"start": v(31.7, -11.15) * mm, "end": v(30.38, -11.15) * mm});
            skLineSegment(sketch, "E376", {"start": v(30.38, -11.15) * mm, "end": v(30.38, -12.11) * mm});
            skLineSegment(sketch, "E377", {"start": v(30.38, -12.11) * mm, "end": v(31.15, -12.11) * mm});
            skLineSegment(sketch, "E378", {"start": v(31.15, -12.11) * mm, "end": v(31.15, -14.96) * mm});
            skLineSegment(sketch, "E379", {"start": v(31.15, -14.96) * mm, "end": v(26.14, -14.96) * mm});
            skLineSegment(sketch, "E380", {"start": v(26.14, -14.96) * mm, "end": v(26.14, -12.11) * mm});
            skLineSegment(sketch, "E381", {"start": v(26.14, -12.11) * mm, "end": v(26.88, -12.11) * mm});
            skLineSegment(sketch, "E382", {"start": v(26.88, -12.11) * mm, "end": v(26.88, -11.15) * mm});
            skLineSegment(sketch, "E383", {"start": v(26.88, -11.15) * mm, "end": v(22.11, -11.15) * mm});
            skLineSegment(sketch, "E384", {"start": v(22.42, -10.84) * mm, "end": v(22.42, -7.56) * mm});
            skLineSegment(sketch, "E385", {"start": v(22.42, -7.56) * mm, "end": v(27.41, -2.57) * mm});
            skLineSegment(sketch, "E386", {"start": v(27.41, -2.57) * mm, "end": v(30.07, -2.57) * mm});
            skLineSegment(sketch, "E387", {"start": v(30.07, -2.57) * mm, "end": v(30.07, -8.61) * mm});
            skLineSegment(sketch, "E388", {"start": v(30.07, -8.61) * mm, "end": v(31.4, -8.61) * mm});
            skLineSegment(sketch, "E389", {"start": v(31.4, -8.61) * mm, "end": v(31.4, -10.84) * mm});
            skLineSegment(sketch, "E390", {"start": v(31.4, -10.84) * mm, "end": v(30.07, -10.84) * mm});
            skLineSegment(sketch, "E391", {"start": v(30.07, -10.84) * mm, "end": v(30.07, -12.42) * mm});
            skLineSegment(sketch, "E392", {"start": v(30.07, -12.42) * mm, "end": v(30.83, -12.42) * mm});
            skLineSegment(sketch, "E393", {"start": v(30.83, -12.42) * mm, "end": v(30.83, -14.65) * mm});
            skLineSegment(sketch, "E394", {"start": v(30.83, -14.65) * mm, "end": v(26.45, -14.65) * mm});
            skLineSegment(sketch, "E395", {"start": v(26.45, -14.65) * mm, "end": v(26.45, -12.42) * mm});
            skLineSegment(sketch, "E396", {"start": v(26.45, -12.42) * mm, "end": v(27.2, -12.42) * mm});
            skLineSegment(sketch, "E397", {"start": v(27.2, -12.42) * mm, "end": v(27.2, -10.84) * mm});
            skLineSegment(sketch, "E398", {"start": v(27.2, -10.84) * mm, "end": v(22.42, -10.84) * mm});
            skLineSegment(sketch, "E399", {"start": v(22.82, -10.44) * mm, "end": v(22.82, -7.72) * mm});
            skLineSegment(sketch, "E400", {"start": v(22.82, -7.72) * mm, "end": v(27.57, -2.97) * mm});
            skLineSegment(sketch, "E401", {"start": v(27.57, -2.97) * mm, "end": v(29.68, -2.97) * mm});
            skLineSegment(sketch, "E402", {"start": v(29.68, -2.97) * mm, "end": v(29.68, -9) * mm});
            skLineSegment(sketch, "E403", {"start": v(29.68, -9) * mm, "end": v(31, -9) * mm});
            skLineSegment(sketch, "E404", {"start": v(31, -9) * mm, "end": v(31, -10.44) * mm});
            skLineSegment(sketch, "E405", {"start": v(31, -10.44) * mm, "end": v(29.68, -10.44) * mm});
            skLineSegment(sketch, "E406", {"start": v(29.68, -10.44) * mm, "end": v(29.68, -12.82) * mm});
            skLineSegment(sketch, "E407", {"start": v(29.68, -12.82) * mm, "end": v(30.44, -12.82) * mm});
            skLineSegment(sketch, "E408", {"start": v(30.44, -12.82) * mm, "end": v(30.44, -14.25) * mm});
            skLineSegment(sketch, "E409", {"start": v(30.44, -14.25) * mm, "end": v(26.85, -14.25) * mm});
            skLineSegment(sketch, "E410", {"start": v(26.85, -14.25) * mm, "end": v(26.85, -12.82) * mm});
            skLineSegment(sketch, "E411", {"start": v(26.85, -12.82) * mm, "end": v(27.59, -12.82) * mm});
            skLineSegment(sketch, "E412", {"start": v(27.59, -12.82) * mm, "end": v(27.59, -10.44) * mm});
            skLineSegment(sketch, "E413", {"start": v(27.59, -10.44) * mm, "end": v(22.82, -10.44) * mm});
            skLineSegment(sketch, "E414", {"start": v(24.9, -9) * mm, "end": v(24.9, -8.36) * mm});
            skLineSegment(sketch, "E415", {"start": v(24.9, -8.36) * mm, "end": v(27.57, -5.7) * mm});
            skLineSegment(sketch, "E416", {"start": v(27.57, -5.7) * mm, "end": v(27.57, -9) * mm});
            skLineSegment(sketch, "E417", {"start": v(27.57, -9) * mm, "end": v(24.9, -9) * mm});
            skLineSegment(sketch, "E418", {"start": v(25.3, -8.6) * mm, "end": v(27.2, -6.7) * mm});
            skLineSegment(sketch, "E419", {"start": v(27.2, -6.7) * mm, "end": v(27.2, -8.6) * mm});
            skLineSegment(sketch, "E420", {"start": v(27.2, -8.6) * mm, "end": v(25.3, -8.6) * mm});
            skLineSegment(sketch, "E421", {"start": v(26.05, -8.28) * mm, "end": v(26.88, -7.45) * mm});
            skLineSegment(sketch, "E422", {"start": v(26.88, -7.45) * mm, "end": v(26.88, -8.28) * mm});
            skLineSegment(sketch, "E423", {"start": v(26.88, -8.28) * mm, "end": v(26.05, -8.28) * mm});
            skLineSegment(sketch, "E424", {"start": v(-43.63, -28.22) * mm, "end": v(-43.63, -23.43) * mm});
            skLineSegment(sketch, "E425", {"start": v(-43.63, -23.43) * mm, "end": v(-33.98, -23.43) * mm});
            skLineSegment(sketch, "E426", {"start": v(-33.98, -23.43) * mm, "end": v(-33.98, -26.3) * mm});
            skLineSegment(sketch, "E427", {"start": v(-33.98, -26.3) * mm, "end": v(-40.15, -26.3) * mm});
            skLineSegment(sketch, "E428", {"start": v(-40.15, -26.3) * mm, "end": v(-40.15, -27) * mm});
            skLineSegment(sketch, "E429", {"start": v(-40.15, -27) * mm, "end": v(-39.73, -27.42) * mm});
            skLineSegment(sketch, "E430", {"start": v(-39.73, -27.42) * mm, "end": v(-35.9, -27.42) * mm});
            skLineSegment(sketch, "E431", {"start": v(-35.9, -27.42) * mm, "end": v(-33.98, -29.34) * mm});
            skLineSegment(sketch, "E432", {"start": v(-33.98, -29.34) * mm, "end": v(-33.98, -34.1) * mm});
            skLineSegment(sketch, "E433", {"start": v(-33.98, -34.1) * mm, "end": v(-36.02, -36.13) * mm});
            skLineSegment(sketch, "E434", {"start": v(-36.02, -36.13) * mm, "end": v(-41.6, -36.13) * mm});
            skLineSegment(sketch, "E435", {"start": v(-41.6, -36.13) * mm, "end": v(-43.63, -34.1) * mm});
            skLineSegment(sketch, "E436", {"start": v(-43.63, -34.1) * mm, "end": v(-43.63, -31.85) * mm});
            skLineSegment(sketch, "E437", {"start": v(-43.63, -31.85) * mm, "end": v(-40.15, -31.85) * mm});
            skLineSegment(sketch, "E438", {"start": v(-40.15, -31.85) * mm, "end": v(-40.15, -32.86) * mm});
            skLineSegment(sketch, "E439", {"start": v(-40.15, -32.86) * mm, "end": v(-39.73, -33.28) * mm});
            skLineSegment(sketch, "E440", {"start": v(-39.73, -33.28) * mm, "end": v(-37.88, -33.28) * mm});
            skLineSegment(sketch, "E441", {"start": v(-37.88, -33.28) * mm, "end": v(-37.48, -32.88) * mm});
            skLineSegment(sketch, "E442", {"start": v(-37.48, -32.88) * mm, "end": v(-37.48, -30.65) * mm});
            skLineSegment(sketch, "E443", {"start": v(-37.48, -30.65) * mm, "end": v(-37.88, -30.25) * mm});
            skLineSegment(sketch, "E444", {"start": v(-37.88, -30.25) * mm, "end": v(-41.6, -30.25) * mm});
            skLineSegment(sketch, "E445", {"start": v(-41.6, -30.25) * mm, "end": v(-43.63, -28.22) * mm});
            skLineSegment(sketch, "E446", {"start": v(-43.34, -28.1) * mm, "end": v(-43.34, -23.72) * mm});
            skLineSegment(sketch, "E447", {"start": v(-43.34, -23.72) * mm, "end": v(-34.27, -23.72) * mm});
            skLineSegment(sketch, "E448", {"start": v(-34.27, -23.72) * mm, "end": v(-34.27, -26) * mm});
            skLineSegment(sketch, "E449", {"start": v(-34.27, -26) * mm, "end": v(-40.44, -26) * mm});
            skLineSegment(sketch, "E450", {"start": v(-40.44, -26) * mm, "end": v(-40.44, -27.12) * mm});
            skLineSegment(sketch, "E451", {"start": v(-40.44, -27.12) * mm, "end": v(-39.85, -27.71) * mm});
            skLineSegment(sketch, "E452", {"start": v(-39.85, -27.71) * mm, "end": v(-36.03, -27.71) * mm});
            skLineSegment(sketch, "E453", {"start": v(-36.03, -27.71) * mm, "end": v(-34.27, -29.46) * mm});
            skLineSegment(sketch, "E454", {"start": v(-34.27, -29.46) * mm, "end": v(-34.27, -33.97) * mm});
            skLineSegment(sketch, "E455", {"start": v(-34.27, -33.97) * mm, "end": v(-36.14, -35.84) * mm});
            skLineSegment(sketch, "E456", {"start": v(-36.14, -35.84) * mm, "end": v(-41.48, -35.84) * mm});
            skLineSegment(sketch, "E457", {"start": v(-41.48, -35.84) * mm, "end": v(-43.34, -33.97) * mm});
            skLineSegment(sketch, "E458", {"start": v(-43.34, -33.97) * mm, "end": v(-43.34, -32.14) * mm});
            skLineSegment(sketch, "E459", {"start": v(-43.34, -32.14) * mm, "end": v(-40.44, -32.14) * mm});
            skLineSegment(sketch, "E460", {"start": v(-40.44, -32.14) * mm, "end": v(-40.44, -32.98) * mm});
            skLineSegment(sketch, "E461", {"start": v(-40.44, -32.98) * mm, "end": v(-39.85, -33.57) * mm});
            skLineSegment(sketch, "E462", {"start": v(-39.85, -33.57) * mm, "end": v(-37.76, -33.57) * mm});
            skLineSegment(sketch, "E463", {"start": v(-37.76, -33.57) * mm, "end": v(-37.2, -33) * mm});
            skLineSegment(sketch, "E464", {"start": v(-37.2, -33) * mm, "end": v(-37.2, -30.53) * mm});
            skLineSegment(sketch, "E465", {"start": v(-37.2, -30.53) * mm, "end": v(-37.76, -29.96) * mm});
            skLineSegment(sketch, "E466", {"start": v(-37.76, -29.96) * mm, "end": v(-41.48, -29.96) * mm});
            skLineSegment(sketch, "E467", {"start": v(-41.48, -29.96) * mm, "end": v(-43.34, -28.1) * mm});
            skLineSegment(sketch, "E468", {"start": v(-42.95, -27.93) * mm, "end": v(-42.95, -24.12) * mm});
            skLineSegment(sketch, "E469", {"start": v(-42.95, -24.12) * mm, "end": v(-34.67, -24.12) * mm});
            skLineSegment(sketch, "E470", {"start": v(-34.67, -24.12) * mm, "end": v(-34.67, -25.6) * mm});
            skLineSegment(sketch, "E471", {"start": v(-34.67, -25.6) * mm, "end": v(-40.84, -25.6) * mm});
            skLineSegment(sketch, "E472", {"start": v(-40.84, -25.6) * mm, "end": v(-40.84, -27.29) * mm});
            skLineSegment(sketch, "E473", {"start": v(-40.84, -27.29) * mm, "end": v(-40.02, -28.1) * mm});
            skLineSegment(sketch, "E474", {"start": v(-40.02, -28.1) * mm, "end": v(-36.2, -28.1) * mm});
            skLineSegment(sketch, "E475", {"start": v(-36.2, -28.1) * mm, "end": v(-34.67, -29.63) * mm});
            skLineSegment(sketch, "E476", {"start": v(-34.67, -29.63) * mm, "end": v(-34.67, -33.8) * mm});
            skLineSegment(sketch, "E477", {"start": v(-34.67, -33.8) * mm, "end": v(-36.3, -35.44) * mm});
            skLineSegment(sketch, "E478", {"start": v(-36.3, -35.44) * mm, "end": v(-41.32, -35.44) * mm});
            skLineSegment(sketch, "E479", {"start": v(-41.32, -35.44) * mm, "end": v(-42.94, -33.8) * mm});
            skLineSegment(sketch, "E480", {"start": v(-42.94, -33.8) * mm, "end": v(-42.94, -32.53) * mm});
            skLineSegment(sketch, "E481", {"start": v(-42.94, -32.53) * mm, "end": v(-40.84, -32.53) * mm});
            skLineSegment(sketch, "E482", {"start": v(-40.84, -32.53) * mm, "end": v(-40.84, -33.15) * mm});
            skLineSegment(sketch, "E483", {"start": v(-40.84, -33.15) * mm, "end": v(-40.02, -33.97) * mm});
            skLineSegment(sketch, "E484", {"start": v(-40.02, -33.97) * mm, "end": v(-37.6, -33.97) * mm});
            skLineSegment(sketch, "E485", {"start": v(-37.6, -33.97) * mm, "end": v(-36.8, -33.16) * mm});
            skLineSegment(sketch, "E486", {"start": v(-36.8, -33.16) * mm, "end": v(-36.8, -30.36) * mm});
            skLineSegment(sketch, "E487", {"start": v(-36.8, -30.36) * mm, "end": v(-37.6, -29.56) * mm});
            skLineSegment(sketch, "E488", {"start": v(-37.6, -29.56) * mm, "end": v(-41.32, -29.56) * mm});
            skLineSegment(sketch, "E489", {"start": v(-41.32, -29.56) * mm, "end": v(-42.95, -27.93) * mm});
            skLineSegment(sketch, "E490", {"start": v(-11.55, -27.04) * mm, "end": v(-11.55, -23.43) * mm});
            skLineSegment(sketch, "E491", {"start": v(-11.55, -23.43) * mm, "end": v(-1.89, -23.43) * mm});
            skLineSegment(sketch, "E492", {"start": v(-1.89, -23.43) * mm, "end": v(-1.89, -25.88) * mm});
            skLineSegment(sketch, "E493", {"start": v(-1.89, -25.88) * mm, "end": v(-5.68, -36.13) * mm});
            skLineSegment(sketch, "E494", {"start": v(-5.68, -36.13) * mm, "end": v(-9.34, -36.13) * mm});
            skLineSegment(sketch, "E495", {"start": v(-9.34, -36.13) * mm, "end": v(-5.7, -26.3) * mm});
            skLineSegment(sketch, "E496", {"start": v(-5.7, -26.3) * mm, "end": v(-8.7, -26.3) * mm});
            skLineSegment(sketch, "E497", {"start": v(-8.7, -26.3) * mm, "end": v(-8.7, -27.04) * mm});
            skLineSegment(sketch, "E498", {"start": v(-8.7, -27.04) * mm, "end": v(-11.55, -27.04) * mm});
            skLineSegment(sketch, "E499", {"start": v(-11.23, -26.72) * mm, "end": v(-11.23, -23.75) * mm});
            skLineSegment(sketch, "E500", {"start": v(-11.23, -23.75) * mm, "end": v(-2.2, -23.75) * mm});
            skLineSegment(sketch, "E501", {"start": v(-2.2, -23.75) * mm, "end": v(-2.2, -25.82) * mm});
            skLineSegment(sketch, "E502", {"start": v(-2.2, -25.82) * mm, "end": v(-5.9, -35.8) * mm});
            skLineSegment(sketch, "E503", {"start": v(-5.9, -35.8) * mm, "end": v(-8.88, -35.8) * mm});
            skLineSegment(sketch, "E504", {"start": v(-8.88, -35.8) * mm, "end": v(-5.24, -25.98) * mm});
            skLineSegment(sketch, "E505", {"start": v(-5.24, -25.98) * mm, "end": v(-9.02, -25.98) * mm});
            skLineSegment(sketch, "E506", {"start": v(-9.02, -25.98) * mm, "end": v(-9.02, -26.72) * mm});
            skLineSegment(sketch, "E507", {"start": v(-9.02, -26.72) * mm, "end": v(-11.23, -26.72) * mm});
            skLineSegment(sketch, "E508", {"start": v(-10.85, -26.34) * mm, "end": v(-10.85, -24.13) * mm});
            skLineSegment(sketch, "E509", {"start": v(-10.85, -24.13) * mm, "end": v(-2.58, -24.13) * mm});
            skLineSegment(sketch, "E510", {"start": v(-2.58, -24.13) * mm, "end": v(-2.58, -25.75) * mm});
            skLineSegment(sketch, "E511", {"start": v(-2.58, -25.75) * mm, "end": v(-6.16, -35.43) * mm});
            skLineSegment(sketch, "E512", {"start": v(-6.16, -35.43) * mm, "end": v(-8.34, -35.43) * mm});
            skLineSegment(sketch, "E513", {"start": v(-8.34, -35.43) * mm, "end": v(-4.7, -25.6) * mm});
            skLineSegment(sketch, "E514", {"start": v(-4.7, -25.6) * mm, "end": v(-9.4, -25.6) * mm});
            skLineSegment(sketch, "E515", {"start": v(-9.4, -25.6) * mm, "end": v(-9.4, -26.34) * mm});
            skLineSegment(sketch, "E516", {"start": v(-9.4, -26.34) * mm, "end": v(-10.85, -26.34) * mm});
            skLineSegment(sketch, "E517", {"start": v(4.52, -28.98) * mm, "end": v(4.52, -25.46) * mm});
            skLineSegment(sketch, "E518", {"start": v(4.52, -25.46) * mm, "end": v(6.55, -23.43) * mm});
            skLineSegment(sketch, "E519", {"start": v(6.55, -23.43) * mm, "end": v(12.1, -23.43) * mm});
            skLineSegment(sketch, "E520", {"start": v(12.1, -23.43) * mm, "end": v(14.13, -25.46) * mm});
            skLineSegment(sketch, "E521", {"start": v(14.13, -25.46) * mm, "end": v(14.13, -28.98) * mm});
            skLineSegment(sketch, "E522", {"start": v(14.13, -28.98) * mm, "end": v(13.33, -29.78) * mm});
            skLineSegment(sketch, "E523", {"start": v(13.33, -29.78) * mm, "end": v(14.13, -30.58) * mm});
            skLineSegment(sketch, "E524", {"start": v(14.13, -30.58) * mm, "end": v(14.13, -34.1) * mm});
            skLineSegment(sketch, "E525", {"start": v(14.13, -34.1) * mm, "end": v(12.1, -36.13) * mm});
            skLineSegment(sketch, "E526", {"start": v(12.1, -36.13) * mm, "end": v(6.55, -36.13) * mm});
            skLineSegment(sketch, "E527", {"start": v(6.55, -36.13) * mm, "end": v(4.52, -34.1) * mm});
            skLineSegment(sketch, "E528", {"start": v(4.52, -34.1) * mm, "end": v(4.52, -30.58) * mm});
            skLineSegment(sketch, "E529", {"start": v(4.52, -30.58) * mm, "end": v(5.32, -29.78) * mm});
            skLineSegment(sketch, "E530", {"start": v(5.32, -29.78) * mm, "end": v(4.52, -28.98) * mm});
            skLineSegment(sketch, "E531", {"start": v(4.83, -28.85) * mm, "end": v(4.83, -25.59) * mm});
            skLineSegment(sketch, "E532", {"start": v(4.83, -25.59) * mm, "end": v(6.68, -23.74) * mm});
            skLineSegment(sketch, "E533", {"start": v(6.68, -23.74) * mm, "end": v(11.97, -23.74) * mm});
            skLineSegment(sketch, "E534", {"start": v(11.97, -23.74) * mm, "end": v(13.82, -25.59) * mm});
            skLineSegment(sketch, "E535", {"start": v(13.82, -25.59) * mm, "end": v(13.82, -28.85) * mm});
            skLineSegment(sketch, "E536", {"start": v(13.82, -28.85) * mm, "end": v(12.9, -29.78) * mm});
            skLineSegment(sketch, "E537", {"start": v(12.9, -29.78) * mm, "end": v(13.82, -30.7) * mm});
            skLineSegment(sketch, "E538", {"start": v(13.82, -30.7) * mm, "end": v(13.82, -33.97) * mm});
            skLineSegment(sketch, "E539", {"start": v(13.82, -33.97) * mm, "end": v(11.97, -35.82) * mm});
            skLineSegment(sketch, "E540", {"start": v(11.97, -35.82) * mm, "end": v(6.68, -35.82) * mm});
            skLineSegment(sketch, "E541", {"start": v(6.68, -35.82) * mm, "end": v(4.83, -33.97) * mm});
            skLineSegment(sketch, "E542", {"start": v(4.83, -33.97) * mm, "end": v(4.83, -30.7) * mm});
            skLineSegment(sketch, "E543", {"start": v(4.83, -30.7) * mm, "end": v(5.75, -29.78) * mm});
            skLineSegment(sketch, "E544", {"start": v(5.75, -29.78) * mm, "end": v(4.83, -28.85) * mm});
            skLineSegment(sketch, "E545", {"start": v(5.23, -28.69) * mm, "end": v(5.23, -25.75) * mm});
            skLineSegment(sketch, "E546", {"start": v(5.23, -25.75) * mm, "end": v(6.84, -24.14) * mm});
            skLineSegment(sketch, "E547", {"start": v(6.84, -24.14) * mm, "end": v(11.8, -24.14) * mm});
            skLineSegment(sketch, "E548", {"start": v(11.8, -24.14) * mm, "end": v(13.42, -25.75) * mm});
            skLineSegment(sketch, "E549", {"start": v(13.42, -25.75) * mm, "end": v(13.42, -28.69) * mm});
            skLineSegment(sketch, "E550", {"start": v(13.42, -28.69) * mm, "end": v(12.33, -29.78) * mm});
            skLineSegment(sketch, "E551", {"start": v(12.33, -29.78) * mm, "end": v(13.42, -30.87) * mm});
            skLineSegment(sketch, "E552", {"start": v(13.42, -30.87) * mm, "end": v(13.42, -33.8) * mm});
            skLineSegment(sketch, "E553", {"start": v(13.42, -33.8) * mm, "end": v(11.8, -35.42) * mm});
            skLineSegment(sketch, "E554", {"start": v(11.8, -35.42) * mm, "end": v(6.84, -35.42) * mm});
            skLineSegment(sketch, "E555", {"start": v(6.84, -35.42) * mm, "end": v(5.23, -33.8) * mm});
            skLineSegment(sketch, "E556", {"start": v(5.23, -33.8) * mm, "end": v(5.23, -30.87) * mm});
            skLineSegment(sketch, "E557", {"start": v(5.23, -30.87) * mm, "end": v(6.32, -29.78) * mm});
            skLineSegment(sketch, "E558", {"start": v(6.32, -29.78) * mm, "end": v(5.23, -28.69) * mm});
            skLineSegment(sketch, "E559", {"start": v(7.48, -26.37) * mm, "end": v(8.25, -25.59) * mm});
            skLineSegment(sketch, "E560", {"start": v(8.25, -25.59) * mm, "end": v(10.4, -25.59) * mm});
            skLineSegment(sketch, "E561", {"start": v(10.4, -25.59) * mm, "end": v(11.16, -26.37) * mm});
            skLineSegment(sketch, "E562", {"start": v(11.16, -26.37) * mm, "end": v(11.16, -28.25) * mm});
            skLineSegment(sketch, "E563", {"start": v(11.16, -28.25) * mm, "end": v(10.4, -29.03) * mm});
            skLineSegment(sketch, "E564", {"start": v(10.4, -29.03) * mm, "end": v(8.25, -29.03) * mm});
            skLineSegment(sketch, "E565", {"start": v(8.25, -29.03) * mm, "end": v(7.48, -28.25) * mm});
            skLineSegment(sketch, "E566", {"start": v(7.48, -28.25) * mm, "end": v(7.48, -26.37) * mm});
            skLineSegment(sketch, "E567", {"start": v(7.87, -26.53) * mm, "end": v(8.42, -25.98) * mm});
            skLineSegment(sketch, "E568", {"start": v(8.42, -25.98) * mm, "end": v(10.23, -25.98) * mm});
            skLineSegment(sketch, "E569", {"start": v(10.23, -25.98) * mm, "end": v(10.77, -26.53) * mm});
            skLineSegment(sketch, "E570", {"start": v(10.77, -26.53) * mm, "end": v(10.77, -28.1) * mm});
            skLineSegment(sketch, "E571", {"start": v(10.77, -28.1) * mm, "end": v(10.23, -28.64) * mm});
            skLineSegment(sketch, "E572", {"start": v(10.23, -28.64) * mm, "end": v(8.42, -28.64) * mm});
            skLineSegment(sketch, "E573", {"start": v(8.42, -28.64) * mm, "end": v(7.87, -28.1) * mm});
            skLineSegment(sketch, "E574", {"start": v(7.87, -28.1) * mm, "end": v(7.87, -26.53) * mm});
            skLineSegment(sketch, "E575", {"start": v(8.19, -26.66) * mm, "end": v(8.55, -26.3) * mm});
            skLineSegment(sketch, "E576", {"start": v(8.55, -26.3) * mm, "end": v(10.1, -26.3) * mm});
            skLineSegment(sketch, "E577", {"start": v(10.1, -26.3) * mm, "end": v(10.45, -26.66) * mm});
            skLineSegment(sketch, "E578", {"start": v(10.45, -26.66) * mm, "end": v(10.45, -27.96) * mm});
            skLineSegment(sketch, "E579", {"start": v(10.45, -27.96) * mm, "end": v(10.1, -28.32) * mm});
            skLineSegment(sketch, "E580", {"start": v(10.1, -28.32) * mm, "end": v(8.55, -28.32) * mm});
            skLineSegment(sketch, "E581", {"start": v(8.55, -28.32) * mm, "end": v(8.19, -27.96) * mm});
            skLineSegment(sketch, "E582", {"start": v(8.19, -27.96) * mm, "end": v(8.19, -26.66) * mm});
            skLineSegment(sketch, "E583", {"start": v(7.87, -33.02) * mm, "end": v(8.42, -33.58) * mm});
            skLineSegment(sketch, "E584", {"start": v(8.42, -33.58) * mm, "end": v(10.23, -33.58) * mm});
            skLineSegment(sketch, "E585", {"start": v(10.23, -33.58) * mm, "end": v(10.77, -33.03) * mm});
            skLineSegment(sketch, "E586", {"start": v(10.77, -33.03) * mm, "end": v(10.77, -31.46) * mm});
            skLineSegment(sketch, "E587", {"start": v(10.77, -31.46) * mm, "end": v(10.23, -30.91) * mm});
            skLineSegment(sketch, "E588", {"start": v(10.23, -30.91) * mm, "end": v(8.42, -30.91) * mm});
            skLineSegment(sketch, "E589", {"start": v(8.42, -30.91) * mm, "end": v(7.87, -31.46) * mm});
            skLineSegment(sketch, "E590", {"start": v(7.87, -31.46) * mm, "end": v(7.87, -33.02) * mm});
            skLineSegment(sketch, "E591", {"start": v(7.48, -33.19) * mm, "end": v(8.25, -33.97) * mm});
            skLineSegment(sketch, "E592", {"start": v(8.25, -33.97) * mm, "end": v(10.4, -33.97) * mm});
            skLineSegment(sketch, "E593", {"start": v(10.4, -33.97) * mm, "end": v(11.16, -33.19) * mm});
            skLineSegment(sketch, "E594", {"start": v(11.16, -33.19) * mm, "end": v(11.16, -31.3) * mm});
            skLineSegment(sketch, "E595", {"start": v(11.16, -31.3) * mm, "end": v(10.4, -30.52) * mm});
            skLineSegment(sketch, "E596", {"start": v(10.4, -30.52) * mm, "end": v(8.25, -30.52) * mm});
            skLineSegment(sketch, "E597", {"start": v(8.25, -30.52) * mm, "end": v(7.48, -31.3) * mm});
            skLineSegment(sketch, "E598", {"start": v(7.48, -31.3) * mm, "end": v(7.48, -33.19) * mm});
            skLineSegment(sketch, "E599", {"start": v(8.19, -32.9) * mm, "end": v(8.55, -33.26) * mm});
            skLineSegment(sketch, "E600", {"start": v(8.55, -33.26) * mm, "end": v(10.1, -33.26) * mm});
            skLineSegment(sketch, "E601", {"start": v(10.1, -33.26) * mm, "end": v(10.45, -32.9) * mm});
            skLineSegment(sketch, "E602", {"start": v(10.45, -32.9) * mm, "end": v(10.45, -31.6) * mm});
            skLineSegment(sketch, "E603", {"start": v(10.45, -31.6) * mm, "end": v(10.1, -31.23) * mm});
            skLineSegment(sketch, "E604", {"start": v(10.1, -31.23) * mm, "end": v(8.55, -31.23) * mm});
            skLineSegment(sketch, "E605", {"start": v(8.55, -31.23) * mm, "end": v(8.19, -31.6) * mm});
            skLineSegment(sketch, "E606", {"start": v(8.19, -31.6) * mm, "end": v(8.19, -32.9) * mm});
            skSolve(sketch);
        }
        {
            var Q0;
            Q0 = qSketchRegion(id + "F0", true);
            var Q1;
            Q1=makeQuery(id+"F0.imprint","IMPRINT",FACE,{"disambiguationData":[TD([[makeQuery(id+"F0.imprint","IMPRINT",EDGE,{"derivedFrom":sQuery(id+"F0.wireOp",EDGE,"E70")}),-1.0]])]});
            var Q2;
            Q2=makeQuery(id+"F0.imprint","IMPRINT",FACE,{"disambiguationData":[TD([[makeQuery(id+"F0.imprint","IMPRINT",EDGE,{"derivedFrom":sQuery(id+"F0.wireOp",EDGE,"E265")}),-1.0]])]});
            var Q3;
            Q3=makeQuery(id+"F0.imprint","IMPRINT",FACE,{"disambiguationData":[TD([[makeQuery(id+"F0.imprint","IMPRINT",EDGE,{"derivedFrom":sQuery(id+"F0.wireOp",EDGE,"E340")}),-1.0]])]});
            var Q4;
            Q4=makeQuery(id+"F0.imprint","IMPRINT",FACE,{"disambiguationData":[TD([[makeQuery(id+"F0.imprint","IMPRINT",EDGE,{"derivedFrom":sQuery(id+"F0.wireOp",EDGE,"E399")}),-1.0]])]});
            var Q5;
            Q5=makeQuery(id+"F0.imprint","IMPRINT",FACE,{"disambiguationData":[TD([[makeQuery(id+"F0.imprint","IMPRINT",EDGE,{"derivedFrom":sQuery(id+"F0.wireOp",EDGE,"E418")}),-1.0]])]});
            var Q6;
            Q6=makeQuery(id+"F0.imprint","IMPRINT",FACE,{"disambiguationData":[TD([[makeQuery(id+"F0.imprint","IMPRINT",EDGE,{"derivedFrom":sQuery(id+"F0.wireOp",EDGE,"E468")}),-1.0]])]});
            var Q7;
            Q7=makeQuery(id+"F0.imprint","IMPRINT",FACE,{"disambiguationData":[TD([[makeQuery(id+"F0.imprint","IMPRINT",EDGE,{"derivedFrom":sQuery(id+"F0.wireOp",EDGE,"E190")}),-1.0]])]});
            var Q8;
            Q8=makeQuery(id+"F0.imprint","IMPRINT",FACE,{"disambiguationData":[TD([[makeQuery(id+"F0.imprint","IMPRINT",EDGE,{"derivedFrom":sQuery(id+"F0.wireOp",EDGE,"E215")}),-1.0]])]});
            var Q9;
            Q9=makeQuery(id+"F0.imprint","IMPRINT",FACE,{"disambiguationData":[TD([[makeQuery(id+"F0.imprint","IMPRINT",EDGE,{"derivedFrom":sQuery(id+"F0.wireOp",EDGE,"E508")}),-1.0]])]});
            var Q10;
            Q10=makeQuery(id+"F0.imprint","IMPRINT",FACE,{"disambiguationData":[TD([[makeQuery(id+"F0.imprint","IMPRINT",EDGE,{"derivedFrom":sQuery(id+"F0.wireOp",EDGE,"E545")}),-1.0]])]});
            var Q11;
            Q11=makeQuery(id+"F0.imprint","IMPRINT",FACE,{"disambiguationData":[TD([[makeQuery(id+"F0.imprint","IMPRINT",EDGE,{"derivedFrom":sQuery(id+"F0.wireOp",EDGE,"E583")}),1.0]])]});
            var Q12;
            Q12=makeQuery(id+"F0.imprint","IMPRINT",FACE,{"disambiguationData":[TD([[makeQuery(id+"F0.imprint","IMPRINT",EDGE,{"derivedFrom":sQuery(id+"F0.wireOp",EDGE,"E567")}),-1.0]])]});
            var Q13;
            Q13=makeQuery(id+"F0.imprint","IMPRINT",FACE,{"disambiguationData":[TD([[makeQuery(id+"F0.imprint","IMPRINT",EDGE,{"derivedFrom":sQuery(id+"F0.wireOp",EDGE,"E115")}),-1.0]])]});
            var Q14;
            Q14=makeQuery(id+"F0.imprint","IMPRINT",FACE,{"disambiguationData":[TD([[makeQuery(id+"F0.imprint","IMPRINT",EDGE,{"derivedFrom":sQuery(id+"F0.wireOp",EDGE,"E140")}),-1.0]])]});
            var Q15;
            Q15=makeQuery(id+"F0.imprint","IMPRINT",FACE,{"disambiguationData":[TD([[makeQuery(id+"F0.imprint","IMPRINT",EDGE,{"derivedFrom":sQuery(id+"F0.wireOp",EDGE,"E16")}),-1.0]])]});
            var Q16;
            Q16=makeQuery(id+"F0.imprint","IMPRINT",FACE,{"disambiguationData":[TD([[makeQuery(id+"F0.imprint","IMPRINT",EDGE,{"derivedFrom":sQuery(id+"F0.wireOp",EDGE,"E32")}),-1.0]])]});
            extrude(context, id + "F1", {"entities" : qUnion([Q0, Q1, Q2, Q3, Q4, Q5, Q6, Q7, Q8, Q9, Q10, Q11, Q12, Q13, Q14, Q15, Q16]), "depth" : 2.54 * mm});
        }
    });
